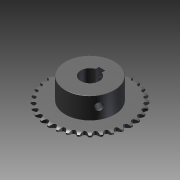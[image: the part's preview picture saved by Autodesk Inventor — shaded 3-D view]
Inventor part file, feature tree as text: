
AUTODESK INVENTOR PART (.ipt)
format: ipt  version: 2011 SP1 (Build 150282100, 282)  size: 487,936 bytes
history: native  units: mm
features: other x14, sketch x5, revolve x3, extrude x2, thread x2
ambient origin geometry x8: Origin, YZ Plane, XZ Plane, XY Plane, X Axis, Y Axis, Z Axis, Center Point
bodies: Solid1 (feature_tree)
feature tree (26):
  revolve  "Revolution1"  [1 undecoded]
  extrude  "Extrusion1"  Depth=9.6585mm TaperAngle=0.0deg
  revolve  "Revolution2"  [1 undecoded]
  thread  "Thread1"  [1 undecoded]
  revolve  "Revolution3"  [1 undecoded]
  thread  "Thread2"  [1 undecoded]
  extrude  "Extrusion2"  [1 undecoded]
  other  "to_screw_1_XY"
  other  "to_screw_1_YZ"
  other  "to_screw_1_ZX"
  other  "to_screw_1_X"
  other  "to_screw_1_Y"
  other  "to_screw_1_Z"
  other  "to_screw_1_Center"
  other  "to_screw_2_XY"
  other  "to_screw_2_YZ"
  other  "to_screw_2_ZX"
  other  "to_screw_2_X"
  other  "to_screw_2_Y"
  other  "to_screw_2_Z"
  other  "to_screw_2_Center"
  sketch  "Sketch_1"  dims[d0=360.0deg d1=2.8mm d2=0.0mm]
  sketch  "Sketch_2"  dims[d3=360.0deg d4=9.6585mm d5=0.0mm]
  sketch  "Sketch_3"  dims[d6=360.0deg d7=11.9585mm d8=0.0mm d9=20.0mm d10=0.0mm]
  sketch  "Sketch_7"
  sketch  "Sketch_5"  dims[d11=0.0mm]
note: 6 required parameter values undecoded (feature->parameter linkage not recoverable at this tier; creation-order binding heuristic only, values carry confidence <= 0.55)